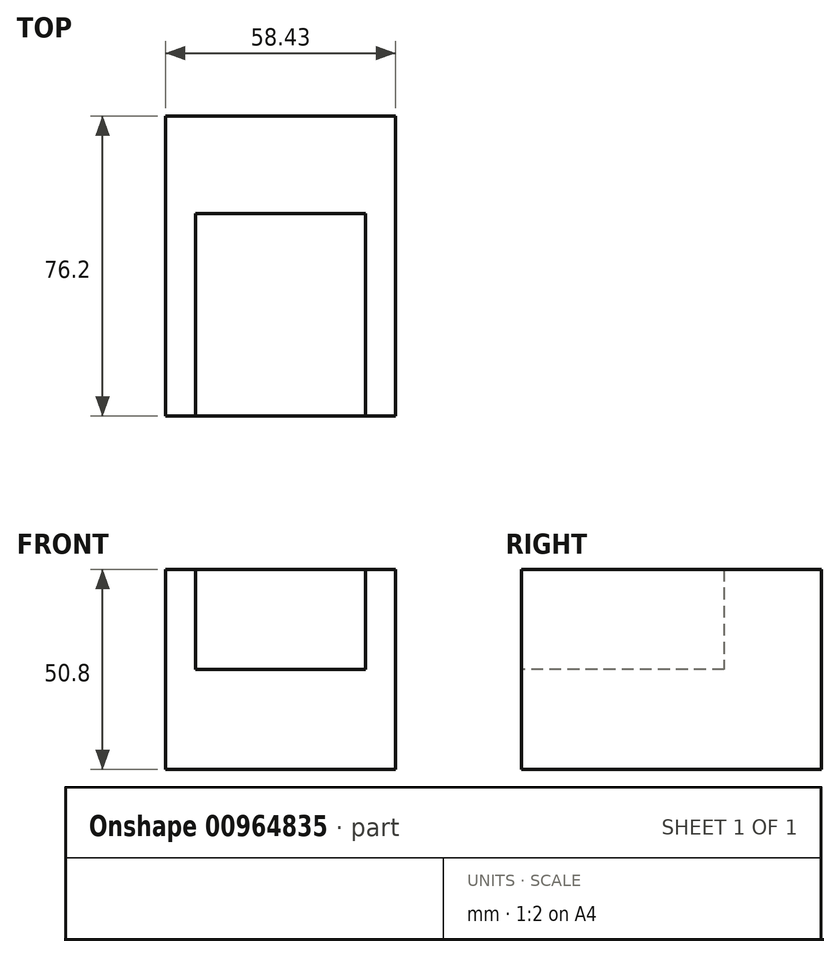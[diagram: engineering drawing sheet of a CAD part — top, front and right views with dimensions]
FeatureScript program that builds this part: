
annotation { "Feature Type Name" : "Feature", "Feature Type Description" : "" }
export const myFeature = defineFeature(function(context is Context, id is Id, definition is map)
    precondition{}
    {
        {
            var Q0;
            Q0=qCreatedBy(makeId("Front.planeOp"),FACE);
            var sketch = newSketch(context, id + "F0", { "sketchPlane" : qUnion([Q0])});
            skLineSegment(sketch, "E0.bottom", {"start": v(0, 0) * mm, "end": v(58.43, 0) * mm});
            skLineSegment(sketch, "E0.top", {"start": v(0, -25.4) * mm, "end": v(58.43, -25.4) * mm});
            skLineSegment(sketch, "E0.left", {"start": v(0, 0) * mm, "end": v(0, -25.4) * mm});
            skLineSegment(sketch, "E0.right", {"start": v(58.43, 0) * mm, "end": v(58.43, -25.4) * mm});
            skSolve(sketch);
        }
        {
            var Q0;
            Q0 = qSketchRegion(id + "F0", true);
            extrude(context, id + "F1", {"entities" : qUnion([Q0]), "depth" : 76.2 * mm, "offsetDistance" : 25.4 * mm});
        }
        {
            var Q0;
            Q0=makeQuery(id+"F1.opExtrude","SWEPT_FACE",FACE,{"disambiguationData":[OSD([sQuery(id+"F0.wireOp",EDGE,"E0.bottom")])]});
            var sketch = newSketch(context, id + "F2", { "sketchPlane" : qUnion([Q0])});
            skLineSegment(sketch, "E1", {"start": v(7.62, -24.73) * mm, "end": v(7.62, -76.2) * mm});
            skLineSegment(sketch, "E2", {"start": v(50.81, -24.73) * mm, "end": v(50.81, -76.2) * mm});
            skLineSegment(sketch, "E3", {"start": v(7.62, -24.73) * mm, "end": v(50.81, -24.73) * mm});
            skSolve(sketch);
        }
        {
            var Q0;
            Q0 = qSketchRegion(id + "F2", true);
            var Q1;
            {var subQ3=sQuery(id+"F2.wireOp",EDGE,"E1");Q1=makeQuery(id+"F2.imprint","IMPRINT",FACE,{"disambiguationData":[TD([[makeQuery(id+"F2.imprint","IMPRINT",EDGE,{"derivedFrom":subQ3}),-1.0]])]});}
            extrude(context, id + "F3", {"entities" : qUnion([Q0, Q1]), "operationType" : NewBodyOperationType.ADD, "depth" : 25.4 * mm, "offsetDistance" : 25.4 * mm});
        }
    });
